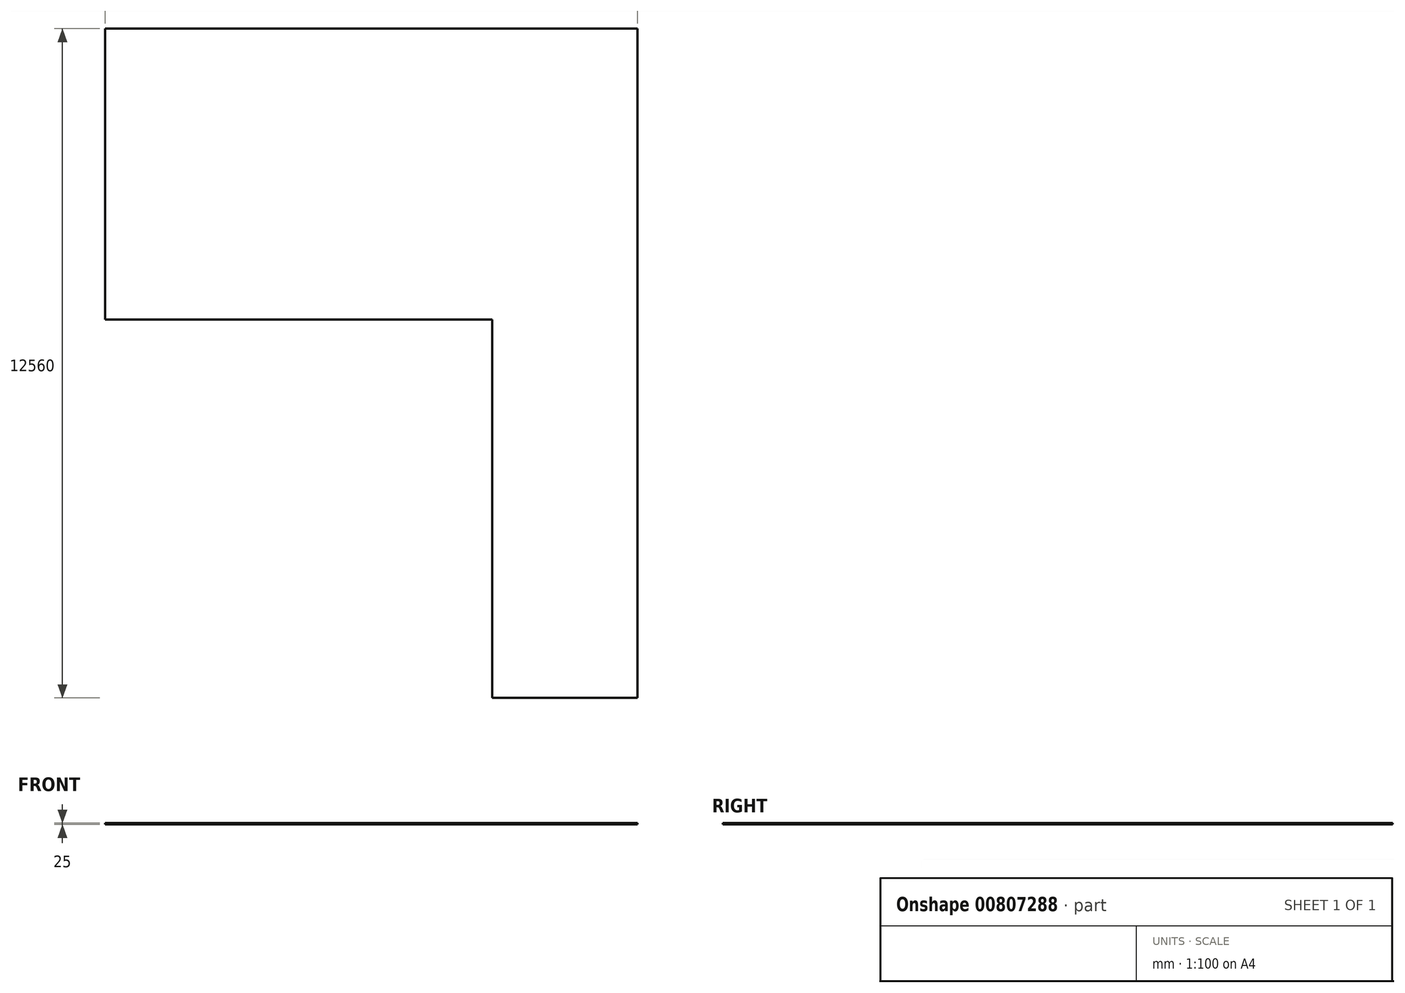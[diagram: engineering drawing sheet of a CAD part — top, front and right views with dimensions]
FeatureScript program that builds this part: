
annotation { "Feature Type Name" : "Feature", "Feature Type Description" : "" }
export const myFeature = defineFeature(function(context is Context, id is Id, definition is map)
    precondition{}
    {
        {
            var Q0;
            Q0=qCreatedBy(makeId("Top.planeOp"),FACE);
            var sketch = newSketch(context, id + "F0", { "sketchPlane" : qUnion([Q0])});
            skLineSegment(sketch, "E0.bottom", {"start": v(-99.88, -7100) * mm, "end": v(2620.12, -7100) * mm});
            skLineSegment(sketch, "E0.top", {"start": v(-7359.88, 5460) * mm, "end": v(2620.12, 5460) * mm});
            skLineSegment(sketch, "E0.left", {"start": v(-7359.88, 0) * mm, "end": v(-7359.88, 5460) * mm});
            skLineSegment(sketch, "E0.right", {"start": v(2620.12, -7100) * mm, "end": v(2620.12, 5460) * mm});
            skLineSegment(sketch, "E1.top", {"start": v(-7359.88, 0) * mm, "end": v(-99.88, 0) * mm});
            skLineSegment(sketch, "E1.right", {"start": v(-99.88, -7100) * mm, "end": v(-99.88, 0) * mm});
            skSolve(sketch);
        }
        {
            var Q0;
            Q0=makeQuery(id+"F0.imprint","IMPRINT",FACE,{"disambiguationData":[TD([[makeQuery(id+"F0.imprint","IMPRINT",EDGE,{"derivedFrom":sQuery(id+"F0.wireOp",EDGE,"E0.bottom")}),1.0]])]});
            extrude(context, id + "F1", {"entities" : qUnion([Q0]), "depth" : 25 * mm, "offsetDistance" : 25 * mm});
        }
    });
